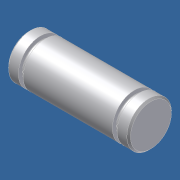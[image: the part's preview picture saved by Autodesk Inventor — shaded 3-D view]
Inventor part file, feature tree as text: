
AUTODESK INVENTOR PART (.ipt)
format: ipt  version: unknown  size: 212,992 bytes
history: native  units: in
note: dims shown in document units (in); Inventor stores cm internally (conversion verified against a paired STEP export)
features: other x49, revolve x1, sketch x1
ambient origin geometry x8: Origin, YZ Plane, XZ Plane, XY Plane, X Axis, Y Axis, Z Axis, Center Point
feature tree (51):
  revolve  "Revolution1"  [1 undecoded]
  other  "p1_XY"
  other  "p1_YZ"
  other  "p1_ZX"
  other  "p1_X"
  other  "p1_Y"
  other  "p1_Z"
  other  "p1_Center"
  other  "p2_XY"
  other  "p2_YZ"
  other  "p2_ZX"
  other  "p2_X"
  other  "p2_Y"
  other  "p2_Z"
  other  "p2_Center"
  other  "pin_XY"
  other  "pin_YZ"
  other  "pin_ZX"
  other  "pin_X"
  other  "pin_Y"
  other  "pin_Z"
  other  "pin_Center"
  other  "rr1_XY"
  other  "rr1_YZ"
  other  "rr1_ZX"
  other  "rr1_X"
  other  "rr1_Y"
  other  "rr1_Z"
  other  "rr1_Center"
  other  "rr2_XY"
  other  "rr2_YZ"
  other  "rr2_ZX"
  other  "rr2_X"
  other  "rr2_Y"
  other  "rr2_Z"
  other  "rr2_Center"
  other  "w21_XY"
  other  "w21_YZ"
  other  "w21_ZX"
  other  "w21_X"
  other  "w21_Y"
  other  "w21_Z"
  other  "w21_Center"
  other  "w22_XY"
  other  "w22_YZ"
  other  "w22_ZX"
  other  "w22_X"
  other  "w22_Y"
  other  "w22_Z"
  other  "w22_Center"
  sketch  "Sketch_1"  dims[d0=360.0deg]
note: 1 required parameter value undecoded (feature->parameter linkage not recoverable at this tier; creation-order binding heuristic only, values carry confidence <= 0.55)
